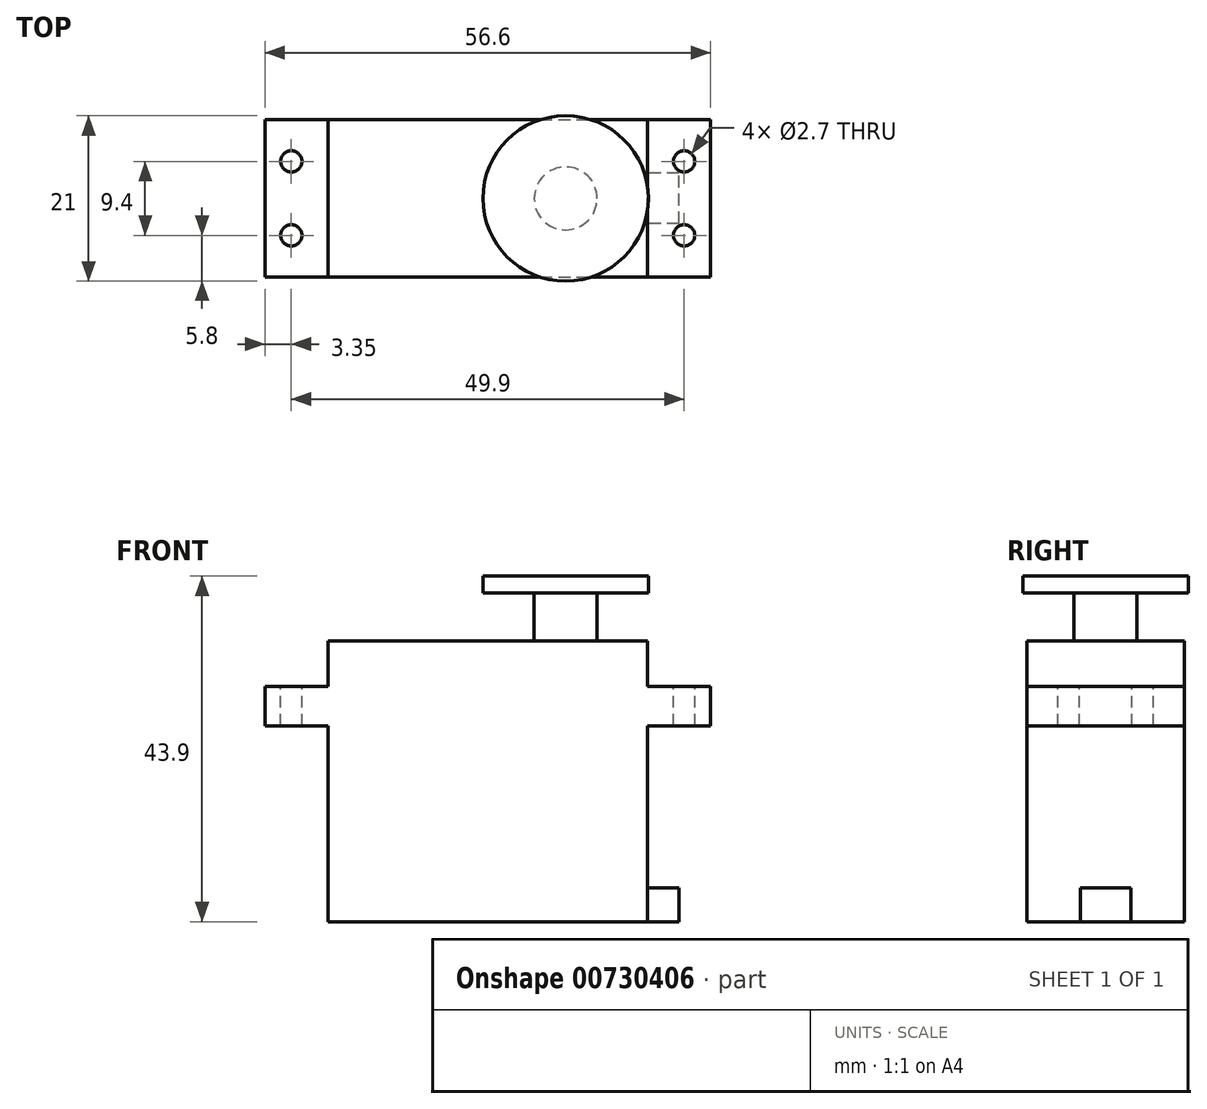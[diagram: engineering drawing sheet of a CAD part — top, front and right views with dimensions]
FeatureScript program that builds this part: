
annotation { "Feature Type Name" : "Feature", "Feature Type Description" : "" }
export const myFeature = defineFeature(function(context is Context, id is Id, definition is map)
    precondition{}
    {
        {
            var Q0;
            Q0=qCreatedBy(makeId("Top.planeOp"),FACE);
            var sketch = newSketch(context, id + "F0", { "sketchPlane" : qUnion([Q0])});
            skLineSegment(sketch, "E0.bottom", {"start": v(0, 0) * mm, "end": v(40.6, 0) * mm});
            skLineSegment(sketch, "E0.top", {"start": v(0, 20) * mm, "end": v(40.6, 20) * mm});
            skLineSegment(sketch, "E0.left", {"start": v(0, 0) * mm, "end": v(0, 20) * mm});
            skLineSegment(sketch, "E0.right", {"start": v(40.6, 0) * mm, "end": v(40.6, 20) * mm});
            skSolve(sketch);
        }
        {
            var Q0;
            Q0 = qSketchRegion(id + "F0", true);
            extrude(context, id + "F1", {"entities" : qUnion([Q0]), "depth" : 35.7 * mm, "offsetDistance" : 25 * mm});
        }
        {
            var Q0;
            Q0=makeQuery(id+"F1.opExtrude","SWEPT_FACE",FACE,{"disambiguationData":[OSD([sQuery(id+"F0.wireOp",EDGE,"E0.bottom")])]});
            var sketch = newSketch(context, id + "F2", { "sketchPlane" : qUnion([Q0])});
            skLineSegment(sketch, "E1.bottom", {"start": v(40.6, 29.9) * mm, "end": v(48.6, 29.9) * mm});
            skLineSegment(sketch, "E1.top", {"start": v(40.6, 24.9) * mm, "end": v(48.6, 24.9) * mm});
            skLineSegment(sketch, "E1.left", {"start": v(40.6, 29.9) * mm, "end": v(40.6, 24.9) * mm});
            skLineSegment(sketch, "E1.right", {"start": v(48.6, 29.9) * mm, "end": v(48.6, 24.9) * mm});
            skLineSegment(sketch, "E2.bottom", {"start": v(0, 29.9) * mm, "end": v(-8, 29.9) * mm});
            skLineSegment(sketch, "E2.top", {"start": v(0, 24.9) * mm, "end": v(-8, 24.9) * mm});
            skLineSegment(sketch, "E2.left", {"start": v(0, 29.9) * mm, "end": v(0, 24.9) * mm});
            skLineSegment(sketch, "E2.right", {"start": v(-8, 29.9) * mm, "end": v(-8, 24.9) * mm});
            skSolve(sketch);
        }
        {
            var Q0;
            Q0 = qSketchRegion(id + "F2", true);
            var Q1;
            Q1=makeQuery(id+"F1.opExtrude","SWEPT_FACE",FACE,{"disambiguationData":[OSD([sQuery(id+"F0.wireOp",EDGE,"E0.top")])]});
            extrude(context, id + "F3", {"entities" : qUnion([Q0]), "operationType" : NewBodyOperationType.ADD, "endBound" : BoundingType.UP_TO_SURFACE, "oppositeDirection" : true, "depth" : 25 * mm, "endBoundEntityFace" : qUnion([Q1]), "offsetDistance" : 25 * mm});
        }
        {
            var Q0;
            Q0=makeQuery(id+"F1.opExtrude","CAP_FACE",FACE,{"disambiguationData":[OSD([sQuery(id+"F0.wireOp",EDGE,"E0.bottom"),sQuery(id+"F0.wireOp",EDGE,"E0.top"),sQuery(id+"F0.wireOp",EDGE,"E0.left"),sQuery(id+"F0.wireOp",EDGE,"E0.right")])],"isStart":false});
            var sketch = newSketch(context, id + "F4", { "sketchPlane" : qUnion([Q0])});
            skCircle(sketch, "E3", {"center": v(30.2, 10) * mm, "radius": 4 * mm});
            skPoint(sketch, "E3.centerSnap0", {"position": v(40.6, 10) * mm});
            skSolve(sketch);
        }
        {
            var Q0;
            Q0 = qSketchRegion(id + "F4", true);
            extrude(context, id + "F5", {"entities" : qUnion([Q0]), "operationType" : NewBodyOperationType.ADD, "depth" : 6.1 * mm, "offsetDistance" : 25 * mm});
        }
        {
            var Q0;
            Q0=makeQuery(id+"F5.opExtrude","CAP_FACE",FACE,{"disambiguationData":[OSD([sQuery(id+"F4.wireOp",EDGE,"E3")])],"isStart":false});
            var sketch = newSketch(context, id + "F6", { "sketchPlane" : qUnion([Q0])});
            skCircle(sketch, "E4", {"center": v(30.2, 10) * mm, "radius": 10.5 * mm});
            skSolve(sketch);
        }
        {
            var Q0;
            Q0 = qSketchRegion(id + "F6", true);
            extrude(context, id + "F7", {"entities" : qUnion([Q0]), "operationType" : NewBodyOperationType.ADD, "depth" : 2.1 * mm, "offsetDistance" : 25 * mm});
        }
        {
            var Q0;
            {var subQ0=sQuery(id+"F2.wireOp",EDGE,"E1.top");var subQ2=sQuery(id+"F0.wireOp",EDGE,"E0.right");Q0=makeQuery(id+"F3.boolean.opBoolean","SPLIT",FACE,{"disambiguationData":[TD([makeQuery(id+"F3.opExtrude","SWEPT_FACE",FACE,{"disambiguationData":[OSD([subQ0])]})])],"derivedFrom":makeQuery(id+"F1.opExtrude","SWEPT_FACE",FACE,{"disambiguationData":[OSD([subQ2])]})});}
            var sketch = newSketch(context, id + "F8", { "sketchPlane" : qUnion([Q0])});
            skLineSegment(sketch, "E5.bottom", {"start": v(13.2, 0) * mm, "end": v(6.8, 0) * mm});
            skLineSegment(sketch, "E5.top", {"start": v(13.2, 4.3) * mm, "end": v(6.8, 4.3) * mm});
            skLineSegment(sketch, "E5.left", {"start": v(13.2, 0) * mm, "end": v(13.2, 4.3) * mm});
            skLineSegment(sketch, "E5.right", {"start": v(6.8, 0) * mm, "end": v(6.8, 4.3) * mm});
            skPoint(sketch, "E5.middle", {"position": v(10, 2.15) * mm});
            skPoint(sketch, "E5.middle.positionSnap0", {"position": v(10, 0) * mm});
            skPoint(sketch, "E5.centerSnap0", {"position": v(10, 0) * mm});
            skSolve(sketch);
        }
        {
            var Q0;
            Q0 = qSketchRegion(id + "F8", true);
            extrude(context, id + "F9", {"entities" : qUnion([Q0]), "operationType" : NewBodyOperationType.ADD, "depth" : 4 * mm, "offsetDistance" : 25 * mm});
        }
        {
            var Q0;
            Q0=makeQuery(id+"F3.opExtrude","SWEPT_FACE",FACE,{"disambiguationData":[OSD([sQuery(id+"F2.wireOp",EDGE,"E2.bottom")])]});
            var sketch = newSketch(context, id + "F10", { "sketchPlane" : qUnion([Q0])});
            skLineSegment(sketch, "E6.bottom", {"start": v(45.25, 14.7) * mm, "end": v(-4.65, 14.7) * mm, "construction": true});
            skLineSegment(sketch, "E6.top", {"start": v(45.25, 5.3) * mm, "end": v(-4.65, 5.3) * mm, "construction": true});
            skLineSegment(sketch, "E6.left", {"start": v(45.25, 14.7) * mm, "end": v(45.25, 5.3) * mm, "construction": true});
            skLineSegment(sketch, "E6.right", {"start": v(-4.65, 14.7) * mm, "end": v(-4.65, 5.3) * mm, "construction": true});
            skPoint(sketch, "E6.middle", {"position": v(20.3, 10) * mm});
            skCircle(sketch, "E7", {"center": v(-4.65, 14.7) * mm, "radius": 1.35 * mm});
            skCircle(sketch, "E8", {"center": v(-4.65, 5.3) * mm, "radius": 1.35 * mm});
            skCircle(sketch, "E9", {"center": v(45.25, 14.7) * mm, "radius": 1.35 * mm});
            skCircle(sketch, "E10", {"center": v(45.25, 5.3) * mm, "radius": 1.35 * mm});
            skSolve(sketch);
        }
        {
            var Q0;
            Q0 = qSketchRegion(id + "F10", true);
            extrude(context, id + "F11", {"entities" : qUnion([Q0]), "operationType" : NewBodyOperationType.REMOVE, "endBound" : BoundingType.UP_TO_NEXT, "oppositeDirection" : true, "depth" : 25 * mm, "offsetDistance" : 25 * mm});
        }
    });
